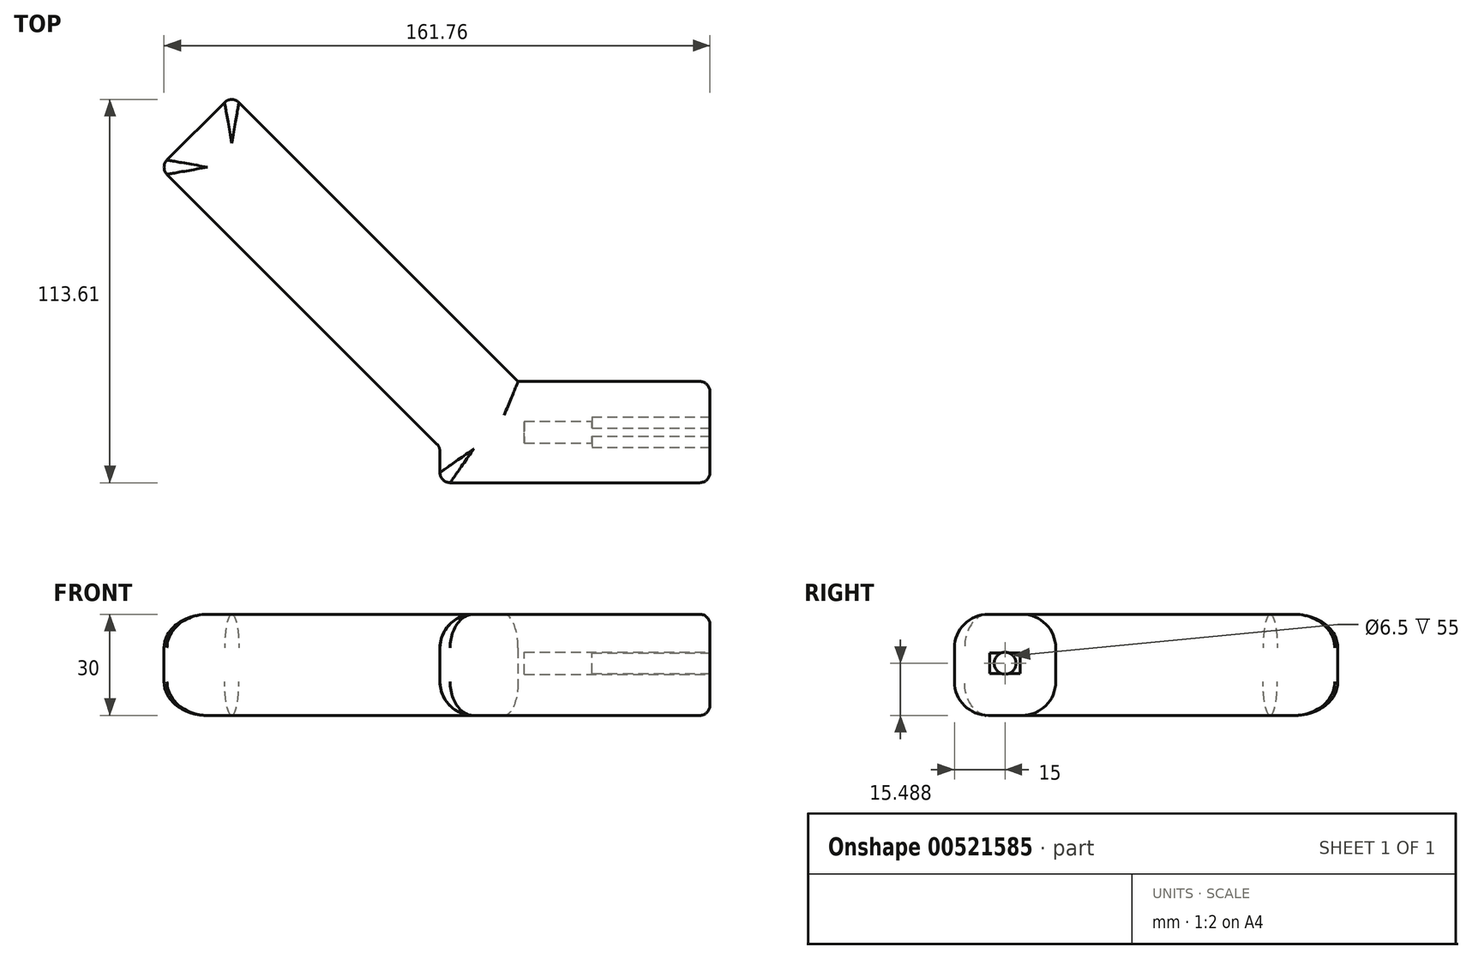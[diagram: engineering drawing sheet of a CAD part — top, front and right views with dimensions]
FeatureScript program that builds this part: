
annotation { "Feature Type Name" : "Feature", "Feature Type Description" : "" }
export const myFeature = defineFeature(function(context is Context, id is Id, definition is map)
    precondition{}
    {
        {
            var Q0;
            Q0=qCreatedBy(makeId("Top.planeOp"),FACE);
            var sketch = newSketch(context, id + "F0", { "sketchPlane" : qUnion([Q0])});
            skLineSegment(sketch, "E0.bottom", {"start": v(40, -15) * mm, "end": v(-40, -15) * mm});
            skLineSegment(sketch, "E0.top", {"start": v(40, 15) * mm, "end": v(-40, 15) * mm});
            skLineSegment(sketch, "E0.left", {"start": v(40, -15) * mm, "end": v(40, 15) * mm});
            skLineSegment(sketch, "E0.right", {"start": v(-40, -15) * mm, "end": v(-40, 15) * mm});
            skPoint(sketch, "E0.middle", {"position": v(0, 0) * mm});
            skLineSegment(sketch, "E1", {"start": v(-16.84, 15) * mm, "end": v(-101.7, 99.85) * mm});
            skLineSegment(sketch, "E2", {"start": v(-101.7, 99.85) * mm, "end": v(-123, 78.55) * mm});
            skLineSegment(sketch, "E3", {"start": v(-123, 78.55) * mm, "end": v(-40, -4.45) * mm});
            skSolve(sketch);
        }
        {
            var Q0;
            Q0=qSketchRegion(id+"F0",true);
            extrude(context, id + "F1", {"entities" : qUnion([Q0]), "depth" : 30 * mm});
        }
        {
            var Q0;
            Q0=makeQuery(id+"F1.opExtrude","SWEPT_EDGE",EDGE,{"disambiguationData":[OSD([sQuery(id+"F0.wireOp",EDGE,"E0.bottom"),sQuery(id+"F0.wireOp",EDGE,"E0.right")])]});
            var Q1;
            Q1=makeQuery(id+"F1.opExtrude","SWEPT_EDGE",EDGE,{"disambiguationData":[OSD([sQuery(id+"F0.wireOp",EDGE,"E0.right"),sQuery(id+"F0.wireOp",EDGE,"E3")])]});
            var Q2;
            Q2=makeQuery(id+"F1.opExtrude","SWEPT_EDGE",EDGE,{"disambiguationData":[OSD([sQuery(id+"F0.wireOp",EDGE,"E2"),sQuery(id+"F0.wireOp",EDGE,"E3")])]});
            var Q3;
            Q3=makeQuery(id+"F1.opExtrude","SWEPT_EDGE",EDGE,{"disambiguationData":[OSD([sQuery(id+"F0.wireOp",EDGE,"E1"),sQuery(id+"F0.wireOp",EDGE,"E2")])]});
            var Q4;
            Q4=makeQuery(id+"F1.opExtrude","SWEPT_EDGE",EDGE,{"disambiguationData":[OSD([sQuery(id+"F0.wireOp",EDGE,"E0.top"),sQuery(id+"F0.wireOp",EDGE,"E0.left")])]});
            var Q5;
            Q5=makeQuery(id+"F1.opExtrude","SWEPT_EDGE",EDGE,{"disambiguationData":[OSD([sQuery(id+"F0.wireOp",EDGE,"E0.bottom"),sQuery(id+"F0.wireOp",EDGE,"E0.left")])]});
            var Q6;
            Q6=makeQuery(id+"F1.opExtrude","CAP_EDGE",EDGE,{"disambiguationData":[OSD([sQuery(id+"F0.wireOp",EDGE,"E0.left")])],"isStart":false});
            var Q7;
            Q7=makeQuery(id+"F1.opExtrude","CAP_EDGE",EDGE,{"disambiguationData":[OSD([sQuery(id+"F0.wireOp",EDGE,"E0.left")])],"isStart":true});
            fillet(context, id + "F2", {"entities" : qUnion([Q0, Q1, Q2, Q3, Q4, Q5, Q6, Q7]), "radius" : 3 * mm, "tangentPropagation" : true});
        }
        {
            var Q0;
            Q0=makeQuery(id+"F1.opExtrude","CAP_EDGE",EDGE,{"disambiguationData":[OSD([sQuery(id+"F0.wireOp",EDGE,"E3")])],"isStart":true});
            var Q1;
            Q1=makeQuery(id+"F1.opExtrude","CAP_EDGE",EDGE,{"disambiguationData":[OSD([sQuery(id+"F0.wireOp",EDGE,"E3")])],"isStart":false});
            var Q2;
            Q2=makeQuery(id+"F1.opExtrude","CAP_EDGE",EDGE,{"disambiguationData":[OSD([sQuery(id+"F0.wireOp",EDGE,"E0.top")])],"isStart":false});
            var Q3;
            Q3=makeQuery(id+"F1.opExtrude","CAP_EDGE",EDGE,{"disambiguationData":[OSD([sQuery(id+"F0.wireOp",EDGE,"E0.top")])],"isStart":true});
            fillet(context, id + "F3", {"entities" : qUnion([Q0, Q1, Q2, Q3]), "radius" : 10 * mm, "tangentPropagation" : true});
        }
        {
            var Q0;
            Q0=makeQuery(id+"F1.opExtrude","SWEPT_FACE",FACE,{"disambiguationData":[OSD([sQuery(id+"F0.wireOp",EDGE,"E0.left")])]});
            var sketch = newSketch(context, id + "F4", { "sketchPlane" : qUnion([Q0])});
            skLineSegment(sketch, "E4.bottom", {"start": v(4.5, 12.49) * mm, "end": v(-4.5, 12.49) * mm});
            skLineSegment(sketch, "E4.top", {"start": v(4.5, 18.49) * mm, "end": v(-4.5, 18.49) * mm});
            skLineSegment(sketch, "E4.left", {"start": v(4.5, 12.49) * mm, "end": v(4.5, 18.49) * mm});
            skLineSegment(sketch, "E4.right", {"start": v(-4.5, 12.49) * mm, "end": v(-4.5, 18.49) * mm});
            skPoint(sketch, "E4.middle", {"position": v(0, 15.49) * mm});
            skSolve(sketch);
        }
        {
            var Q0;
            Q0=qSketchRegion(id+"F4",true);
            extrude(context, id + "F5", {"entities" : qUnion([Q0]), "operationType" : NewBodyOperationType.REMOVE, "oppositeDirection" : true, "depth" : 35 * mm});
        }
        {
            var Q0;
            Q0=makeQuery(id+"F5.boolean.opBoolean","COPY",FACE,{"derivedFrom":makeQuery(id+"F5.opExtrude","CAP_FACE",FACE,{"disambiguationData":[OSD([sQuery(id+"F4.wireOp",EDGE,"E4.bottom"),sQuery(id+"F4.wireOp",EDGE,"E4.top"),sQuery(id+"F4.wireOp",EDGE,"E4.left"),sQuery(id+"F4.wireOp",EDGE,"E4.right")])],"isStart":false})});
            var sketch = newSketch(context, id + "F6", { "sketchPlane" : qUnion([Q0])});
            skCircle(sketch, "E5", {"center": v(0, 15.49) * mm, "radius": 3.25 * mm});
            skSolve(sketch);
        }
        {
            var Q0;
            Q0=qSketchRegion(id+"F6",true);
            extrude(context, id + "F7", {"entities" : qUnion([Q0]), "operationType" : NewBodyOperationType.REMOVE, "oppositeDirection" : true, "offsetDistance" : 25.4 * mm, "depth" : 20 * mm, "hasSecondDirection" : true, "secondDirectionOppositeDirection" : false, "secondDirectionDepth" : 40 * mm});
        }
    });
